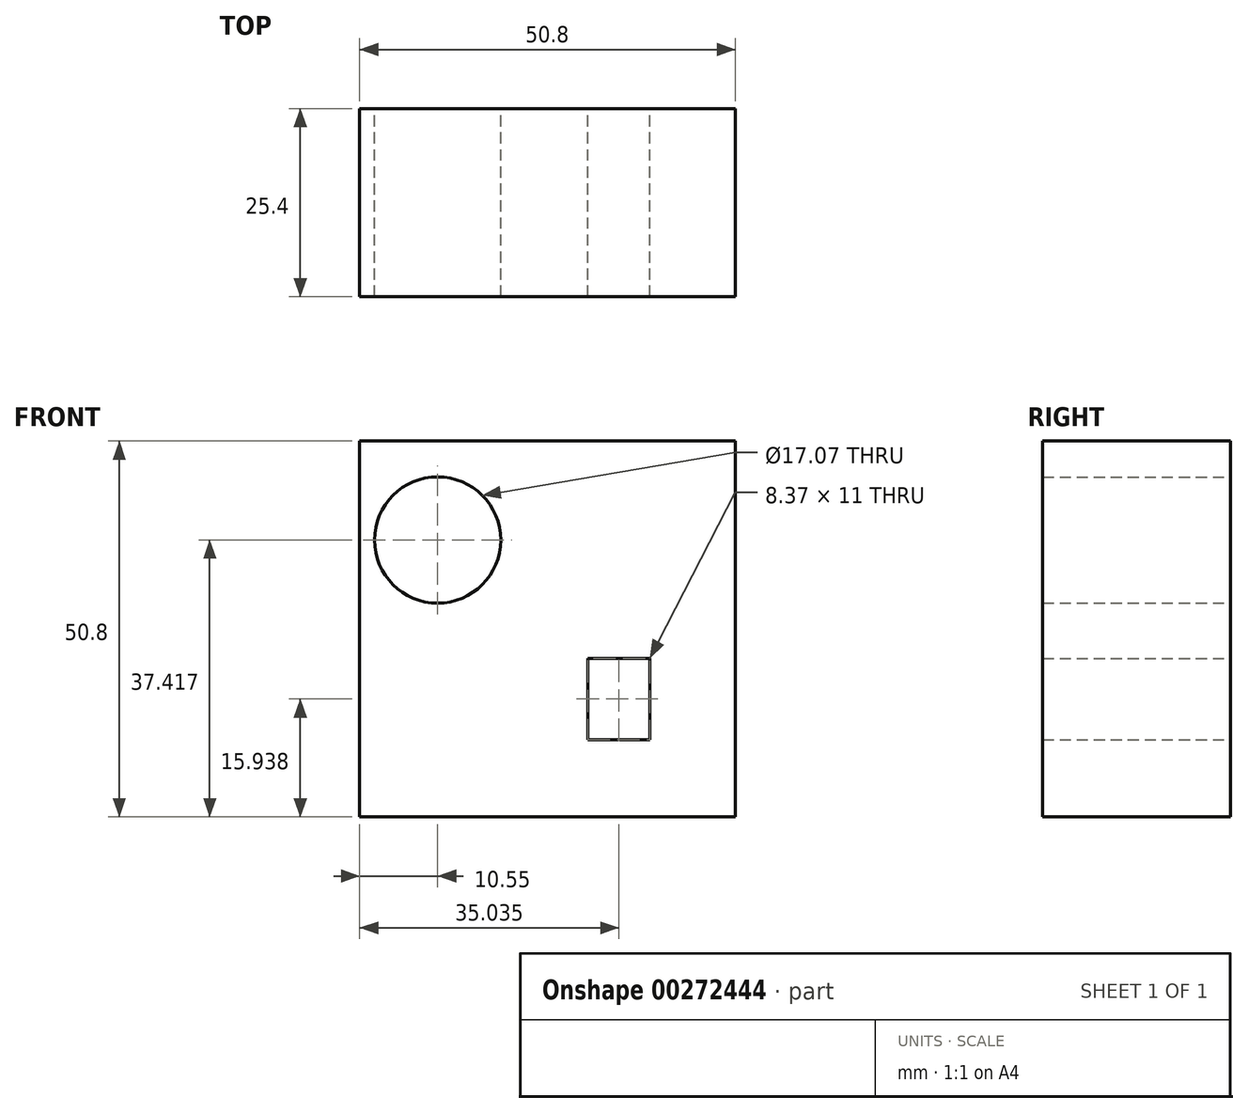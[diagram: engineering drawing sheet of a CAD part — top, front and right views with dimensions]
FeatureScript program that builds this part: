
annotation { "Feature Type Name" : "Feature", "Feature Type Description" : "" }
export const myFeature = defineFeature(function(context is Context, id is Id, definition is map)
    precondition{}
    {
        {
            var Q0;
            Q0=qCreatedBy(makeId("Front.planeOp"),FACE);
            var sketch = newSketch(context, id + "F0", { "sketchPlane" : qUnion([Q0])});
            skLineSegment(sketch, "E0.bottom", {"start": v(-10.55, 20.3) * mm, "end": v(40.25, 20.3) * mm});
            skLineSegment(sketch, "E0.top", {"start": v(-10.55, -30.5) * mm, "end": v(40.25, -30.5) * mm});
            skLineSegment(sketch, "E0.left", {"start": v(-10.55, 20.3) * mm, "end": v(-10.55, -30.5) * mm});
            skLineSegment(sketch, "E0.right", {"start": v(40.25, 20.3) * mm, "end": v(40.25, -30.5) * mm});
            skCircle(sketch, "E1", {"center": v(0, 6.92) * mm, "radius": 8.53 * mm});
            skLineSegment(sketch, "E2.bottom", {"start": v(20.3, -20.06) * mm, "end": v(28.67, -20.06) * mm});
            skLineSegment(sketch, "E2.top", {"start": v(20.3, -9.06) * mm, "end": v(28.67, -9.06) * mm});
            skLineSegment(sketch, "E2.left", {"start": v(20.3, -20.06) * mm, "end": v(20.3, -9.06) * mm});
            skLineSegment(sketch, "E2.right", {"start": v(28.67, -20.06) * mm, "end": v(28.67, -9.06) * mm});
            skSolve(sketch);
        }
        {
            var Q0;
            Q0 = qSketchRegion(id + "F0", true);
            extrude(context, id + "F1", {"entities" : qUnion([Q0]), "depth" : 25.4 * mm});
        }
    });
